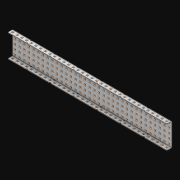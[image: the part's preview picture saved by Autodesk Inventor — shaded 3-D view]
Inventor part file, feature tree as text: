
AUTODESK INVENTOR PART (.ipt)
format: ipt  version: 2021 (Build 250183000, 183)  size: 3,929,088 bytes
history: native  units: in
note: dims shown in document units (in); Inventor stores cm internally (conversion verified against a paired STEP export)
features: extrude x239, other x238, sketch x4, thicken_offset x3, pattern_linear x3, imported_body x1
ambient origin geometry x8: Origin, YZ Plane, XZ Plane, XY Plane, X Axis, Y Axis, Z Axis, Center Point
bodies: Solid1 (feature_tree)
feature tree (488):
  thicken_offset  "Thicken1"
  thicken_offset  "Thicken2"
  thicken_offset  "Thicken3"
  pattern_linear  "Rectangular Pattern1"  Spacing1=0.001in  [1 undecoded]
  pattern_linear  "Rectangular Pattern2"  Spacing1=0.001in  [1 undecoded]
  pattern_linear  "Rectangular Pattern3"  Spacing1=0.182in  [1 undecoded]
  extrude  "Extrusion1"  Depth=0.063in TaperAngle=0.0deg
  sketch  "Sketch1"  dims[d0=0.001in]
  other  "Srf1"
  sketch  "Sketch2"  dims[d1=0.001in]
  other  "Srf2"
  sketch  "Sketch3"  dims[d2=0.001in]
  other  "Srf3"
  other  "Srf4"
  other  "Srf5"
  other  "Srf6"
  other  "Srf7"
  other  "Srf8"
  other  "Srf9"
  other  "Srf10"
  other  "Srf11"
  other  "Srf12"
  other  "Srf13"
  other  "Srf14"
  other  "Srf15"
  other  "Srf16"
  other  "Srf17"
  other  "Srf18"
  other  "Srf19"
  other  "Srf20"
  other  "Srf21"
  other  "Srf22"
  other  "Srf23"
  other  "Srf24"
  other  "Srf25"
  other  "Srf26"
  other  "Srf27"
  other  "Srf28"
  other  "Srf29"
  other  "Srf30"
  other  "Srf31"
  other  "Srf32"
  other  "Srf33"
  other  "Srf34"
  other  "Srf35"
  other  "Srf36"
  other  "Srf38"
  other  "Srf39"
  other  "Srf40"
  other  "Srf41"
  other  "Srf42"
  other  "Srf43"
  other  "Srf44"
  other  "Srf45"
  other  "Srf46"
  other  "Srf47"
  other  "Srf48"
  other  "Srf49"
  other  "Srf50"
  other  "Srf51"
  other  "Srf52"
  other  "Srf53"
  other  "Srf54"
  other  "Srf55"
  other  "Srf56"
  other  "Srf57"
  other  "Srf58"
  other  "Srf59"
  other  "Srf60"
  other  "Srf61"
  other  "Srf62"
  other  "Srf63"
  other  "Srf64"
  other  "Srf65"
  other  "Srf66"
  other  "Srf67"
  other  "Srf68"
  other  "Srf69"
  other  "Srf70"
  other  "Srf72"
  other  "Srf73"
  other  "Srf74"
  other  "Srf75"
  other  "Srf76"
  other  "Srf77"
  other  "Srf78"
  other  "Srf79"
  other  "Srf80"
  other  "Srf81"
  other  "Srf82"
  other  "Srf83"
  other  "Srf84"
  other  "Srf85"
  other  "Srf86"
  other  "Srf87"
  other  "Srf88"
  other  "Srf89"
  other  "Srf90"
  other  "Srf91"
  other  "Srf92"
  other  "Srf93"
  other  "Srf94"
  other  "Srf95"
  other  "Srf96"
  other  "Srf97"
  other  "Srf98"
  other  "Srf99"
  other  "Srf100"
  other  "Srf101"
  other  "Srf102"
  other  "Srf103"
  other  "Srf104"
  other  "Srf106"
  other  "Srf107"
  other  "Srf108"
  other  "Srf109"
  other  "Srf110"
  other  "Srf111"
  other  "Srf112"
  other  "Srf113"
  other  "Srf114"
  other  "Srf115"
  other  "Srf116"
  other  "Srf117"
  other  "Srf118"
  other  "Srf119"
  other  "Srf120"
  other  "Srf121"
  other  "Srf122"
  other  "Srf123"
  other  "Srf124"
  other  "Srf125"
  other  "Srf126"
  other  "Srf127"
  other  "Srf128"
  other  "Srf129"
  other  "Srf130"
  other  "Srf131"
  other  "Srf132"
  other  "Srf133"
  other  "Srf134"
  other  "Srf135"
  other  "Srf136"
  other  "Srf137"
  other  "Srf138"
  other  "Srf139"
  other  "Srf141"
  other  "Srf142"
  other  "Srf143"
  other  "Srf144"
  other  "Srf145"
  other  "Srf146"
  other  "Srf147"
  other  "Srf148"
  other  "Srf149"
  other  "Srf150"
  other  "Srf151"
  other  "Srf152"
  other  "Srf153"
  other  "Srf154"
  other  "Srf155"
  other  "Srf156"
  other  "Srf157"
  other  "Srf158"
  other  "Srf159"
  other  "Srf160"
  other  "Srf161"
  other  "Srf162"
  other  "Srf163"
  other  "Srf164"
  other  "Srf165"
  other  "Srf166"
  other  "Srf167"
  other  "Srf168"
  other  "Srf169"
  other  "Srf170"
  other  "Srf171"
  other  "Srf172"
  other  "Srf173"
  other  "Srf174"
  other  "Srf176"
  other  "Srf177"
  other  "Srf178"
  other  "Srf179"
  other  "Srf180"
  other  "Srf181"
  other  "Srf182"
  other  "Srf183"
  other  "Srf184"
  other  "Srf185"
  other  "Srf186"
  other  "Srf187"
  other  "Srf188"
  other  "Srf189"
  other  "Srf190"
  other  "Srf191"
  other  "Srf192"
  other  "Srf193"
  other  "Srf194"
  other  "Srf195"
  other  "Srf196"
  other  "Srf197"
  other  "Srf198"
  other  "Srf199"
  other  "Srf200"
  other  "Srf201"
  other  "Srf202"
  other  "Srf203"
  other  "Srf204"
  other  "Srf205"
  other  "Srf206"
  other  "Srf207"
  other  "Srf208"
  other  "Srf209"
  other  "Srf211"
  other  "Srf212"
  other  "Srf213"
  other  "Srf214"
  other  "Srf215"
  other  "Srf216"
  other  "Srf217"
  other  "Srf218"
  other  "Srf219"
  other  "Srf220"
  other  "Srf221"
  other  "Srf222"
  other  "Srf223"
  other  "Srf224"
  other  "Srf225"
  other  "Srf226"
  other  "Srf227"
  other  "Srf228"
  other  "Srf229"
  other  "Srf230"
  other  "Srf231"
  other  "Srf232"
  other  "Srf233"
  other  "Srf234"
  other  "Srf235"
  other  "Srf236"
  other  "Srf237"
  other  "Srf238"
  other  "Srf239"
  other  "Srf240"
  other  "Srf241"
  other  "Srf242"
  other  "Srf243"
  other  "Srf244"
  sketch  "Sketch4"  dims[d3=0.001in d4=0.001in d5=0.001in d6=0.182in d7=0.063in d8=0.0in d9=0.182in d10=0.063in d11=0.0in d12=0.182in d13=0.063in d14=0.0in d17=0.5in d18=13.3858in d20=0.5in d21=13.3858in d23=0.5in d24=1.9685in d26=0.5in d27=0.5in d28=0.0in]
  imported_body  "Imported1"
  extrude  "ExtrusionSrf1"  Depth=0.5in
  extrude  "ExtrusionSrf2"  Depth=0.063in TaperAngle=0.0deg
  extrude  "ExtrusionSrf3"  Depth=0.5in
  extrude  "ExtrusionSrf4"  Depth=0.063in TaperAngle=0.0deg
  extrude  "ExtrusionSrf5"  Depth=0.5in
  extrude  "ExtrusionSrf6"  Depth=0.5in
  extrude  "ExtrusionSrf7"  Depth=0.5in
  extrude  "ExtrusionSrf8"  Depth=0.5in
  extrude  "ExtrusionSrf9"  Depth=0.5in
  extrude  "ExtrusionSrf10"  Depth=0.5in
  extrude  "ExtrusionSrf11"  Depth=0.5in
  extrude  "ExtrusionSrf12"  TaperAngle=0.0deg  [1 undecoded]
  extrude  "ExtrusionSrf13"  [1 undecoded]
  extrude  "ExtrusionSrf14"  [1 undecoded]
  extrude  "ExtrusionSrf15"  [1 undecoded]
  extrude  "ExtrusionSrf16"  [1 undecoded]
  extrude  "ExtrusionSrf17"  [1 undecoded]
  extrude  "ExtrusionSrf18"  [1 undecoded]
  extrude  "ExtrusionSrf19"  [1 undecoded]
  extrude  "ExtrusionSrf20"  [1 undecoded]
  extrude  "ExtrusionSrf21"  [1 undecoded]
  extrude  "ExtrusionSrf22"  [1 undecoded]
  extrude  "ExtrusionSrf23"  [1 undecoded]
  extrude  "ExtrusionSrf24"  [1 undecoded]
  extrude  "ExtrusionSrf25"  [1 undecoded]
  extrude  "ExtrusionSrf26"  [1 undecoded]
  extrude  "ExtrusionSrf27"  [1 undecoded]
  extrude  "ExtrusionSrf28"  [1 undecoded]
  extrude  "ExtrusionSrf29"  [1 undecoded]
  extrude  "ExtrusionSrf30"  [1 undecoded]
  extrude  "ExtrusionSrf31"  [1 undecoded]
  extrude  "ExtrusionSrf32"  [1 undecoded]
  extrude  "ExtrusionSrf33"  [1 undecoded]
  extrude  "ExtrusionSrf34"  [1 undecoded]
  extrude  "ExtrusionSrf35"  [1 undecoded]
  extrude  "ExtrusionSrf36"  [1 undecoded]
  extrude  "ExtrusionSrf38"  [1 undecoded]
  extrude  "ExtrusionSrf39"  [1 undecoded]
  extrude  "ExtrusionSrf40"  [1 undecoded]
  extrude  "ExtrusionSrf41"  [1 undecoded]
  extrude  "ExtrusionSrf42"  [1 undecoded]
  extrude  "ExtrusionSrf43"  [1 undecoded]
  extrude  "ExtrusionSrf44"  [1 undecoded]
  extrude  "ExtrusionSrf45"  [1 undecoded]
  extrude  "ExtrusionSrf46"  [1 undecoded]
  extrude  "ExtrusionSrf47"  [1 undecoded]
  extrude  "ExtrusionSrf48"  [1 undecoded]
  extrude  "ExtrusionSrf49"  [1 undecoded]
  extrude  "ExtrusionSrf50"  [1 undecoded]
  extrude  "ExtrusionSrf51"  [1 undecoded]
  extrude  "ExtrusionSrf52"  [1 undecoded]
  extrude  "ExtrusionSrf53"  [1 undecoded]
  extrude  "ExtrusionSrf54"  [1 undecoded]
  extrude  "ExtrusionSrf55"  [1 undecoded]
  extrude  "ExtrusionSrf56"  [1 undecoded]
  extrude  "ExtrusionSrf57"  [1 undecoded]
  extrude  "ExtrusionSrf58"  [1 undecoded]
  extrude  "ExtrusionSrf59"  [1 undecoded]
  extrude  "ExtrusionSrf60"  [1 undecoded]
  extrude  "ExtrusionSrf61"  [1 undecoded]
  extrude  "ExtrusionSrf62"  [1 undecoded]
  extrude  "ExtrusionSrf63"  [1 undecoded]
  extrude  "ExtrusionSrf64"  [1 undecoded]
  extrude  "ExtrusionSrf65"  [1 undecoded]
  extrude  "ExtrusionSrf66"  [1 undecoded]
  extrude  "ExtrusionSrf67"  [1 undecoded]
  extrude  "ExtrusionSrf68"  [1 undecoded]
  extrude  "ExtrusionSrf69"  [1 undecoded]
  extrude  "ExtrusionSrf70"  [1 undecoded]
  extrude  "ExtrusionSrf72"  [1 undecoded]
  extrude  "ExtrusionSrf73"  [1 undecoded]
  extrude  "ExtrusionSrf74"  [1 undecoded]
  extrude  "ExtrusionSrf75"  [1 undecoded]
  extrude  "ExtrusionSrf76"  [1 undecoded]
  extrude  "ExtrusionSrf77"  [1 undecoded]
  extrude  "ExtrusionSrf78"  [1 undecoded]
  extrude  "ExtrusionSrf79"  [1 undecoded]
  extrude  "ExtrusionSrf80"  [1 undecoded]
  extrude  "ExtrusionSrf81"  [1 undecoded]
  extrude  "ExtrusionSrf82"  [1 undecoded]
  extrude  "ExtrusionSrf83"  [1 undecoded]
  extrude  "ExtrusionSrf84"  [1 undecoded]
  extrude  "ExtrusionSrf85"  [1 undecoded]
  extrude  "ExtrusionSrf86"  [1 undecoded]
  extrude  "ExtrusionSrf87"  [1 undecoded]
  extrude  "ExtrusionSrf88"  [1 undecoded]
  extrude  "ExtrusionSrf89"  [1 undecoded]
  extrude  "ExtrusionSrf90"  [1 undecoded]
  extrude  "ExtrusionSrf91"  [1 undecoded]
  extrude  "ExtrusionSrf92"  [1 undecoded]
  extrude  "ExtrusionSrf93"  [1 undecoded]
  extrude  "ExtrusionSrf94"  [1 undecoded]
  extrude  "ExtrusionSrf95"  [1 undecoded]
  extrude  "ExtrusionSrf96"  [1 undecoded]
  extrude  "ExtrusionSrf97"  [1 undecoded]
  extrude  "ExtrusionSrf98"  [1 undecoded]
  extrude  "ExtrusionSrf99"  [1 undecoded]
  extrude  "ExtrusionSrf100"  [1 undecoded]
  extrude  "ExtrusionSrf101"  [1 undecoded]
  extrude  "ExtrusionSrf102"  [1 undecoded]
  extrude  "ExtrusionSrf103"  [1 undecoded]
  extrude  "ExtrusionSrf104"  [1 undecoded]
  extrude  "ExtrusionSrf106"  [1 undecoded]
  extrude  "ExtrusionSrf107"  [1 undecoded]
  extrude  "ExtrusionSrf108"  [1 undecoded]
  extrude  "ExtrusionSrf109"  [1 undecoded]
  extrude  "ExtrusionSrf110"  [1 undecoded]
  extrude  "ExtrusionSrf111"  [1 undecoded]
  extrude  "ExtrusionSrf112"  [1 undecoded]
  extrude  "ExtrusionSrf113"  [1 undecoded]
  extrude  "ExtrusionSrf114"  [1 undecoded]
  extrude  "ExtrusionSrf115"  [1 undecoded]
  extrude  "ExtrusionSrf116"  [1 undecoded]
  extrude  "ExtrusionSrf117"  [1 undecoded]
  extrude  "ExtrusionSrf118"  [1 undecoded]
  extrude  "ExtrusionSrf119"  [1 undecoded]
  extrude  "ExtrusionSrf120"  [1 undecoded]
  extrude  "ExtrusionSrf121"  [1 undecoded]
  extrude  "ExtrusionSrf122"  [1 undecoded]
  extrude  "ExtrusionSrf123"  [1 undecoded]
  extrude  "ExtrusionSrf124"  [1 undecoded]
  extrude  "ExtrusionSrf125"  [1 undecoded]
  extrude  "ExtrusionSrf126"  [1 undecoded]
  extrude  "ExtrusionSrf127"  [1 undecoded]
  extrude  "ExtrusionSrf128"  [1 undecoded]
  extrude  "ExtrusionSrf129"  [1 undecoded]
  extrude  "ExtrusionSrf130"  [1 undecoded]
  extrude  "ExtrusionSrf131"  [1 undecoded]
  extrude  "ExtrusionSrf132"  [1 undecoded]
  extrude  "ExtrusionSrf133"  [1 undecoded]
  extrude  "ExtrusionSrf134"  [1 undecoded]
  extrude  "ExtrusionSrf135"  [1 undecoded]
  extrude  "ExtrusionSrf136"  [1 undecoded]
  extrude  "ExtrusionSrf137"  [1 undecoded]
  extrude  "ExtrusionSrf138"  [1 undecoded]
  extrude  "ExtrusionSrf139"  [1 undecoded]
  extrude  "ExtrusionSrf141"  [1 undecoded]
  extrude  "ExtrusionSrf142"  [1 undecoded]
  extrude  "ExtrusionSrf143"  [1 undecoded]
  extrude  "ExtrusionSrf144"  [1 undecoded]
  extrude  "ExtrusionSrf145"  [1 undecoded]
  extrude  "ExtrusionSrf146"  [1 undecoded]
  extrude  "ExtrusionSrf147"  [1 undecoded]
  extrude  "ExtrusionSrf148"  [1 undecoded]
  extrude  "ExtrusionSrf149"  [1 undecoded]
  extrude  "ExtrusionSrf150"  [1 undecoded]
  extrude  "ExtrusionSrf151"  [1 undecoded]
  extrude  "ExtrusionSrf152"  [1 undecoded]
  extrude  "ExtrusionSrf153"  [1 undecoded]
  extrude  "ExtrusionSrf154"  [1 undecoded]
  extrude  "ExtrusionSrf155"  [1 undecoded]
  extrude  "ExtrusionSrf156"  [1 undecoded]
  extrude  "ExtrusionSrf157"  [1 undecoded]
  extrude  "ExtrusionSrf158"  [1 undecoded]
  extrude  "ExtrusionSrf159"  [1 undecoded]
  extrude  "ExtrusionSrf160"  [1 undecoded]
  extrude  "ExtrusionSrf161"  [1 undecoded]
  extrude  "ExtrusionSrf162"  [1 undecoded]
  extrude  "ExtrusionSrf163"  [1 undecoded]
  extrude  "ExtrusionSrf164"  [1 undecoded]
  extrude  "ExtrusionSrf165"  [1 undecoded]
  extrude  "ExtrusionSrf166"  [1 undecoded]
  extrude  "ExtrusionSrf167"  [1 undecoded]
  extrude  "ExtrusionSrf168"  [1 undecoded]
  extrude  "ExtrusionSrf169"  [1 undecoded]
  extrude  "ExtrusionSrf170"  [1 undecoded]
  extrude  "ExtrusionSrf171"  [1 undecoded]
  extrude  "ExtrusionSrf172"  [1 undecoded]
  extrude  "ExtrusionSrf173"  [1 undecoded]
  extrude  "ExtrusionSrf174"  [1 undecoded]
  extrude  "ExtrusionSrf176"  [1 undecoded]
  extrude  "ExtrusionSrf177"  [1 undecoded]
  extrude  "ExtrusionSrf178"  [1 undecoded]
  extrude  "ExtrusionSrf179"  [1 undecoded]
  extrude  "ExtrusionSrf180"  [1 undecoded]
  extrude  "ExtrusionSrf181"  [1 undecoded]
  extrude  "ExtrusionSrf182"  [1 undecoded]
  extrude  "ExtrusionSrf183"  [1 undecoded]
  extrude  "ExtrusionSrf184"  [1 undecoded]
  extrude  "ExtrusionSrf185"  [1 undecoded]
  extrude  "ExtrusionSrf186"  [1 undecoded]
  extrude  "ExtrusionSrf187"  [1 undecoded]
  extrude  "ExtrusionSrf188"  [1 undecoded]
  extrude  "ExtrusionSrf189"  [1 undecoded]
  extrude  "ExtrusionSrf190"  [1 undecoded]
  extrude  "ExtrusionSrf191"  [1 undecoded]
  extrude  "ExtrusionSrf192"  [1 undecoded]
  extrude  "ExtrusionSrf193"  [1 undecoded]
  extrude  "ExtrusionSrf194"  [1 undecoded]
  extrude  "ExtrusionSrf195"  [1 undecoded]
  extrude  "ExtrusionSrf196"  [1 undecoded]
  extrude  "ExtrusionSrf197"  [1 undecoded]
  extrude  "ExtrusionSrf198"  [1 undecoded]
  extrude  "ExtrusionSrf199"  [1 undecoded]
  extrude  "ExtrusionSrf200"  [1 undecoded]
  extrude  "ExtrusionSrf201"  [1 undecoded]
  extrude  "ExtrusionSrf202"  [1 undecoded]
  extrude  "ExtrusionSrf203"  [1 undecoded]
  extrude  "ExtrusionSrf204"  [1 undecoded]
  extrude  "ExtrusionSrf205"  [1 undecoded]
  extrude  "ExtrusionSrf206"  [1 undecoded]
  extrude  "ExtrusionSrf207"  [1 undecoded]
  extrude  "ExtrusionSrf208"  [1 undecoded]
  extrude  "ExtrusionSrf209"  [1 undecoded]
  extrude  "ExtrusionSrf211"  [1 undecoded]
  extrude  "ExtrusionSrf212"  [1 undecoded]
  extrude  "ExtrusionSrf213"  [1 undecoded]
  extrude  "ExtrusionSrf214"  [1 undecoded]
  extrude  "ExtrusionSrf215"  [1 undecoded]
  extrude  "ExtrusionSrf216"  [1 undecoded]
  extrude  "ExtrusionSrf217"  [1 undecoded]
  extrude  "ExtrusionSrf218"  [1 undecoded]
  extrude  "ExtrusionSrf219"  [1 undecoded]
  extrude  "ExtrusionSrf220"  [1 undecoded]
  extrude  "ExtrusionSrf221"  [1 undecoded]
  extrude  "ExtrusionSrf222"  [1 undecoded]
  extrude  "ExtrusionSrf223"  [1 undecoded]
  extrude  "ExtrusionSrf224"  [1 undecoded]
  extrude  "ExtrusionSrf225"  [1 undecoded]
  extrude  "ExtrusionSrf226"  [1 undecoded]
  extrude  "ExtrusionSrf227"  [1 undecoded]
  extrude  "ExtrusionSrf228"  [1 undecoded]
  extrude  "ExtrusionSrf229"  [1 undecoded]
  extrude  "ExtrusionSrf230"  [1 undecoded]
  extrude  "ExtrusionSrf231"  [1 undecoded]
  extrude  "ExtrusionSrf232"  [1 undecoded]
  extrude  "ExtrusionSrf233"  [1 undecoded]
  extrude  "ExtrusionSrf234"  [1 undecoded]
  extrude  "ExtrusionSrf235"  [1 undecoded]
  extrude  "ExtrusionSrf236"  [1 undecoded]
  extrude  "ExtrusionSrf237"  [1 undecoded]
  extrude  "ExtrusionSrf238"  [1 undecoded]
  extrude  "ExtrusionSrf239"  [1 undecoded]
  extrude  "ExtrusionSrf240"  [1 undecoded]
  extrude  "ExtrusionSrf241"  [1 undecoded]
  extrude  "ExtrusionSrf242"  [1 undecoded]
  extrude  "ExtrusionSrf243"  [1 undecoded]
  extrude  "ExtrusionSrf244"  [1 undecoded]
note: 230 required parameter values undecoded (feature->parameter linkage not recoverable at this tier; creation-order binding heuristic only, values carry confidence <= 0.55)
